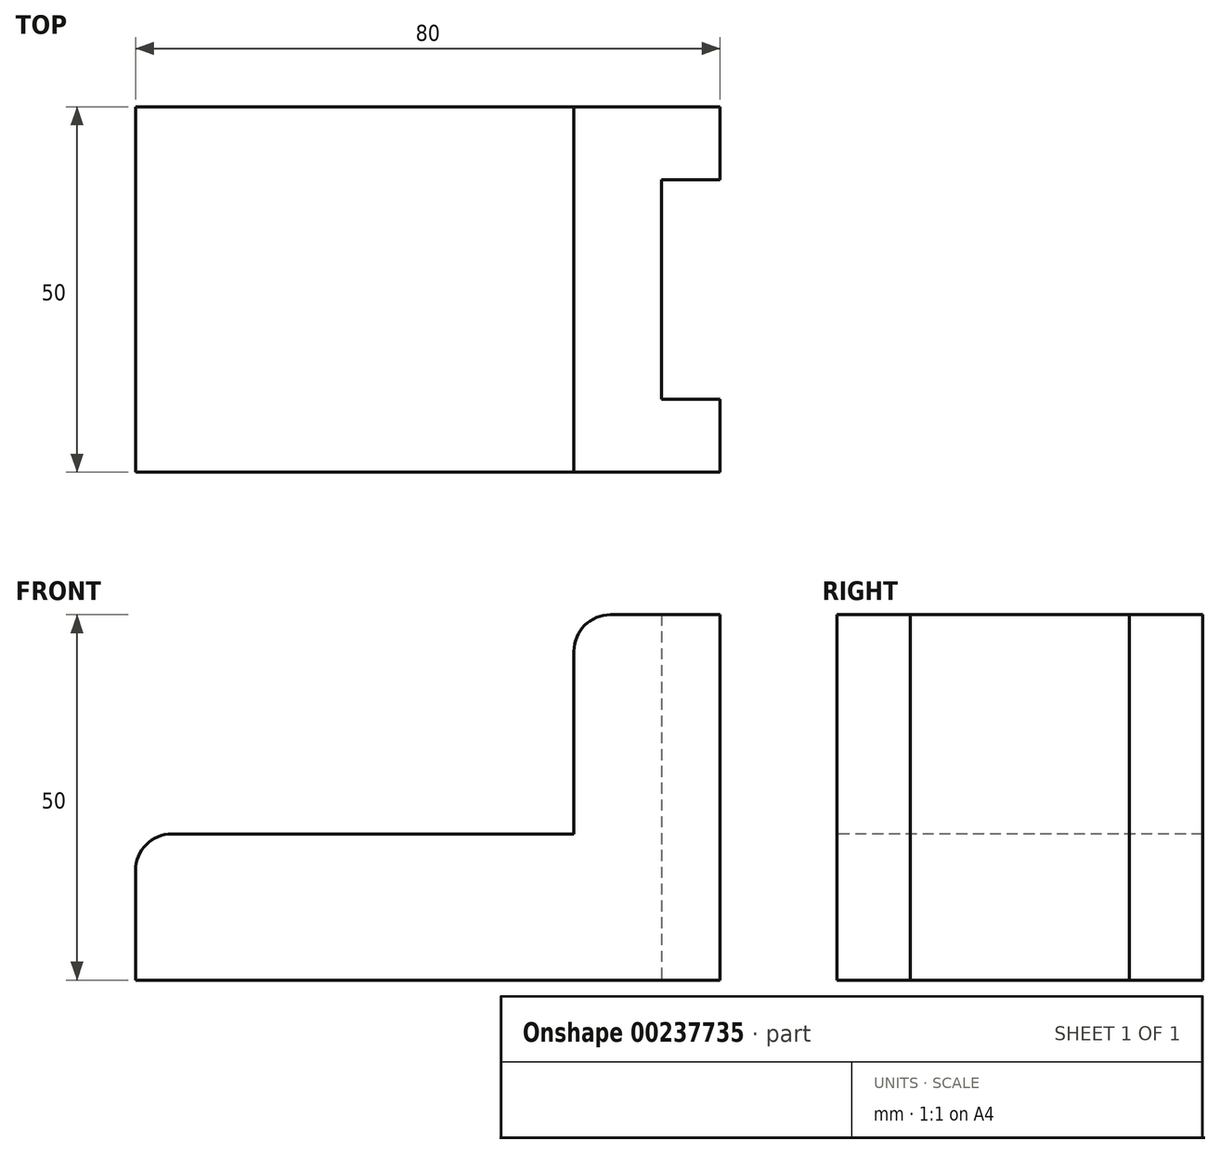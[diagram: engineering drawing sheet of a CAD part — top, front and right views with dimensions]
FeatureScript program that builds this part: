
annotation { "Feature Type Name" : "Feature", "Feature Type Description" : "" }
export const myFeature = defineFeature(function(context is Context, id is Id, definition is map)
    precondition{}
    {
        {
            var Q0;
            Q0=qCreatedBy(makeId("Top.planeOp"),FACE);
            var sketch = newSketch(context, id + "F0", { "sketchPlane" : qUnion([Q0])});
            skLineSegment(sketch, "E0", {"start": v(-60, 7.22) * mm, "end": v(20, 7.22) * mm});
            skLineSegment(sketch, "E1", {"start": v(20, 7.22) * mm, "end": v(20, 57.22) * mm});
            skLineSegment(sketch, "E2", {"start": v(20, 57.22) * mm, "end": v(-60, 57.22) * mm});
            skLineSegment(sketch, "E3", {"start": v(-60, 57.22) * mm, "end": v(-60, 7.22) * mm});
            skLineSegment(sketch, "E4", {"start": v(0, 57.22) * mm, "end": v(0, 7.22) * mm});
            skLineSegment(sketch, "E5", {"start": v(20, 47.22) * mm, "end": v(12, 47.22) * mm});
            skLineSegment(sketch, "E6", {"start": v(12, 47.22) * mm, "end": v(12, 17.22) * mm});
            skLineSegment(sketch, "E7", {"start": v(12, 17.22) * mm, "end": v(20, 17.22) * mm});
            skSolve(sketch);
        }
        {
            var Q0;
            {var subQ0=sQuery(id+"F0.wireOp",EDGE,"E3");Q0=makeQuery(id+"F0.imprint","IMPRINT",FACE,{"disambiguationData":[TD([[makeQuery(id+"F0.imprint","IMPRINT",EDGE,{"derivedFrom":subQ0}),1.0]])]});}
            extrude(context, id + "F1", {"entities" : qUnion([Q0]), "depth" : 20 * mm});
        }
        {
            var Q0;
            {var subQ3=sQuery(id+"F0.wireOp",EDGE,"E4");Q0=makeQuery(id+"F0.imprint","IMPRINT",FACE,{"disambiguationData":[TD([[makeQuery(id+"F0.imprint","IMPRINT",EDGE,{"derivedFrom":subQ3}),1.0]])]});}
            extrude(context, id + "F2", {"entities" : qUnion([Q0]), "operationType" : NewBodyOperationType.ADD, "depth" : 50 * mm});
        }
        {
            var Q0;
            Q0=makeQuery(id+"F2.opExtrude","CAP_EDGE",EDGE,{"disambiguationData":[OSD([sQuery(id+"F0.wireOp",EDGE,"E4")])],"isStart":false});
            var Q1;
            Q1=makeQuery(id+"F1.opExtrude","CAP_EDGE",EDGE,{"disambiguationData":[OSD([sQuery(id+"F0.wireOp",EDGE,"E3")])],"isStart":false});
            fillet(context, id + "F3", {"entities" : qUnion([Q0, Q1]), "radius" : 5 * mm, "tangentPropagation" : true, "allowEdgeOverflow" : false});
        }
    });
